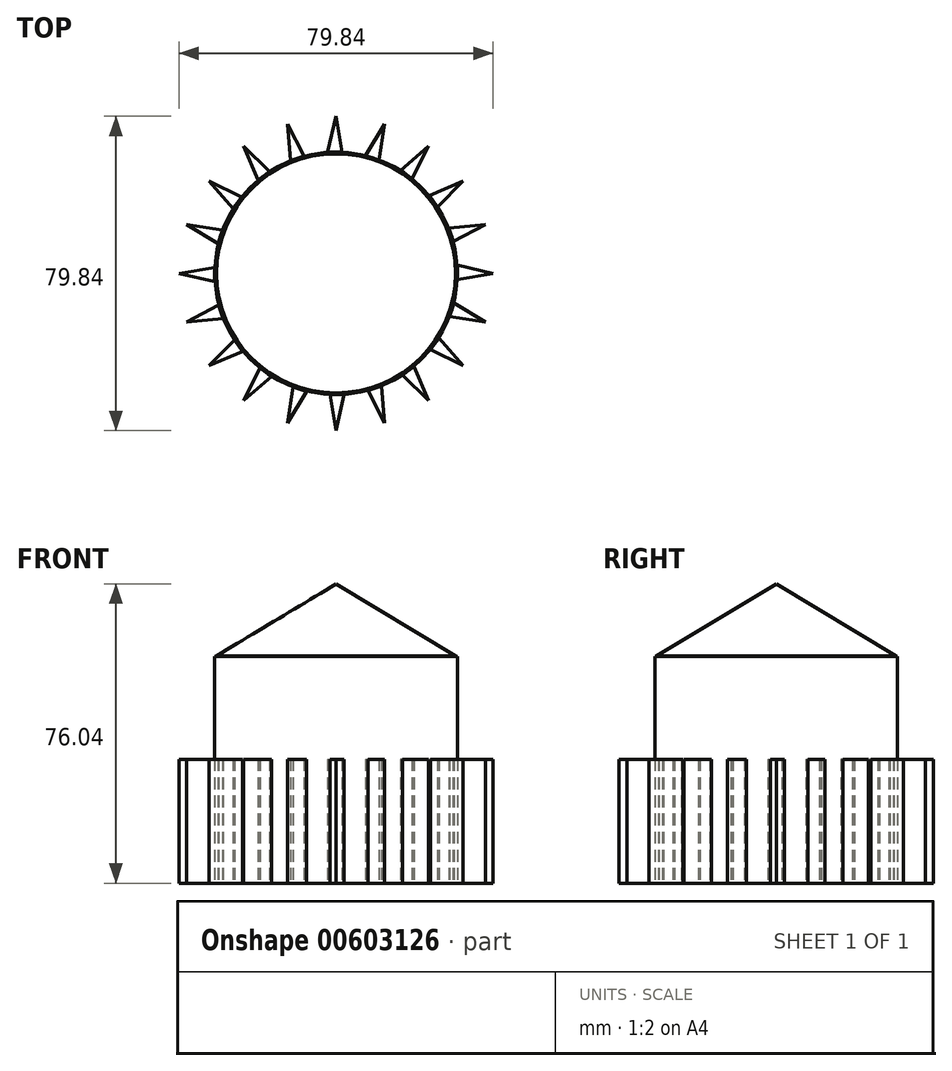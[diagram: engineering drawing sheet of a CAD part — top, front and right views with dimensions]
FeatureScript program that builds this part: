
annotation { "Feature Type Name" : "Feature", "Feature Type Description" : "" }
export const myFeature = defineFeature(function(context is Context, id is Id, definition is map)
    precondition{}
    {
        {
            var Q0;
            Q0=qCreatedBy(makeId("Top.planeOp"),FACE);
            var sketch = newSketch(context, id + "F0", { "sketchPlane" : qUnion([Q0])});
            skCircle(sketch, "E0", {"center": v(0, 0) * mm, "radius": 30.8 * mm});
            skSolve(sketch);
        }
        {
            var Q0;
            Q0=makeQuery(id+"F0.imprint","IMPRINT",FACE,{"disambiguationData":[TD([[makeQuery(id+"F0.imprint","IMPRINT",EDGE,{"derivedFrom":sQuery(id+"F0.wireOp",EDGE,"E0")}),1.0]])]});
            extrude(context, id + "F1", {"entities" : qUnion([Q0]), "depth" : 57.66 * mm, "offsetDistance" : 25.4 * mm});
        }
        {
            var Q0;
            Q0=qCreatedBy(makeId("Front.planeOp"),FACE);
            var sketch = newSketch(context, id + "F2", { "sketchPlane" : qUnion([Q0])});
            skLineSegment(sketch, "E1", {"start": v(0, 76.04) * mm, "end": v(-30.37, 57.76) * mm});
            skLineSegment(sketch, "E2", {"start": v(-30.37, 57.76) * mm, "end": v(0, 57.76) * mm});
            skLineSegment(sketch, "E3", {"start": v(0, 57.76) * mm, "end": v(0, 76.04) * mm});
            skSolve(sketch);
        }
        {
            var Q0;
            Q0=makeQuery(id+"F2.imprint","IMPRINT",FACE,{"disambiguationData":[TD([[makeQuery(id+"F2.imprint","IMPRINT",EDGE,{"derivedFrom":sQuery(id+"F2.wireOp",EDGE,"E1")}),1.0]])]});
            var Q1;
            Q1=sQuery(id+"F2.wireOp",EDGE,"E3");
            revolve(context, id + "F3", {"entities" : qUnion([Q0]), "axis" : qUnion([Q1]), "revolveType" : RevolveType.FULL});
        }
        {
            var Q0;
            Q0=qCreatedBy(makeId("Top.planeOp"),FACE);
            var sketch = newSketch(context, id + "F4", { "sketchPlane" : qUnion([Q0])});
            skLineSegment(sketch, "E4", {"start": v(-1.52, -30.82) * mm, "end": v(2.1, -30.82) * mm});
            skLineSegment(sketch, "E5", {"start": v(2.1, -30.82) * mm, "end": v(0, -39.92) * mm});
            skLineSegment(sketch, "E6", {"start": v(0, -39.92) * mm, "end": v(-1.52, -30.82) * mm});
            skSolve(sketch);
        }
        {
            var Q0;
            Q0=makeQuery(id+"F4.imprint","IMPRINT",FACE,{"disambiguationData":[TD([[makeQuery(id+"F4.imprint","IMPRINT",EDGE,{"derivedFrom":sQuery(id+"F4.wireOp",EDGE,"E4")}),-1.0]])]});
            extrude(context, id + "F5", {"entities" : qUnion([Q0]), "depth" : 31.5 * mm, "offsetDistance" : 25.4 * mm});
        }
        {
            var Q0;
            Q0=makeQuery(id+"F5.opExtrude","SWEPT_BODY",BODY,{"disambiguationData":[OSD([sQuery(id+"F4.wireOp",EDGE,"E4"),sQuery(id+"F4.wireOp",EDGE,"E5"),sQuery(id+"F4.wireOp",EDGE,"E6")])]});
            var Q1;
            Q1=makeQuery(id+"F1.opExtrude","SWEPT_FACE",FACE,{"disambiguationData":[OSD([sQuery(id+"F0.wireOp",EDGE,"E0")])]});
            circularPattern(context, id + "F6", {"entities" : qUnion([Q0]), "axis" : qUnion([Q1]), "angle" : 360 * degree, "instanceCount" : 20, "equalSpace" : true});
        }
    });
